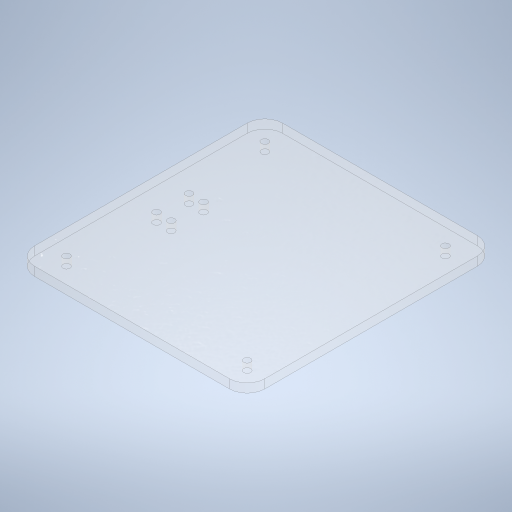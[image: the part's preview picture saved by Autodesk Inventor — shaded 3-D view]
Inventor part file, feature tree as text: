
AUTODESK INVENTOR PART (.ipt)
format: ipt  version: 2023.1 (Build 271208000, 208)  size: 281,088 bytes
history: native  units: mm
features: extrude x1, fillet x1, sketch x1
ambient origin geometry x8: Origin, YZ Plane, XZ Plane, XY Plane, X Axis, Y Axis, Z Axis, Center Point
bodies: Solid1 (feature_tree)
feature tree (3):
  extrude  "Extrusion1"  Depth=130.0mm
  fillet  "Fillet1"  Radius=4.0mm
  sketch  "Sketch1"  dims[d0=140.0mm d1=130.0mm d2=4.0mm d3=14.0mm d4=14.0mm d5=70.0mm d6=65.0mm d9=18.0mm d10=4.0mm d11=9.15mm d12=4.0mm d13=9.15mm d14=8.25mm d15=5.0mm d16=0.0mm d17=10.0mm]
